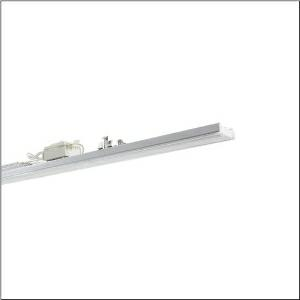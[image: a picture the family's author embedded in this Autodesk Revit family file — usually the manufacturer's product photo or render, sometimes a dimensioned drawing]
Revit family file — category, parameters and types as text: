
# Revit family: licross_21_recessed_ho_52te11cn4c5s
name_source: partatom
category: Lighting Fixtures
units: mm (PartAtom-declared; Revit-internal decimal feet)

## family parameters
Cut with Voids When Loaded = No
Host = Face
Light Source = No
Part Type = Normal
Room Calculation Point = No
Round Connector Dimension = Use Diameter
Shared = No

## types (1)
- --- (1 x LED, 12640 lm, 68.4 W, 4000K)
    Apparent Load = 68 VA
    CIE Flux Codes = 87 95 99 100 100
    Color Rendering = 80
    Color Temperature = 4000K
    Default Elevation = 1800 mm
    Description = Licross 21 Recessed HO, luminaire insert, of sheet steel, galvanised, coil coated, white, length: 1.500mm, width: 66mm, height: 67mm, LED rated luminous flux: 12.640lm, light colour: 840, SDCM (Standard Deviation of Colour Matching)MacAdam ≤ 3 SDCM (initial), control gear: ON/OFF Multilumen, CLOi, with plug, 3-pole, with phase selection, mains connection: 220..240V, AC, 50/60Hz, start of lifetime: 68W, end of service life: 83W, internal wiring halogen-free, primary light control with lens, of plastic, primary optical cover: cover, of PMMA, light emission: direct distribution, primary light characteristic: symmetric, protection rating (complete): IP54, insulation class (complete): insulation class I (protective earthing), certification: CE, ENEC, VDE, UKCA, protection symbol: D if used in an environment with non-conductive dust loads with corresponding accessories, impact resistance: IK06, permissible ambient temperature for indoor applications: -35..+30°C, corresponds to IFS (International Featured Standards) requirements for safety and quality in the food industry, reducing of maximum allowable ambient temperature of 5°C with ceiling mounting, LABS conformity tested according to VDMA 24364:2018-05, The light source and the operating device comply with the requirements of the Ecodesign Regulation (EU) 2019/2020 and are replaceable in accordance with this regulation, packaging unit: 1 piece
    Height = 58 mm
    Lamp = 1 x LED
    Lamp Light Flux = 12640 lm
    Lamp Power = 68.4 W
    Lamp count = 1
    Length = 1500 mm
    Luminous efficacy = 185 lm/W
    Manufacturer = Siteco
    ModVariant = No
    Model = 52TE11CN4C5S
    Mounting Place = Ceiling
    Mounting Type = Pendant
    Number of Poles = 1
    OnlyDefault = Yes
    Power Factor = 1
    Product Name = Licross 21 Recessed HO
    Product group = luminaire insert | ceiling pendant
    ProductGroupID = 901
    Protection Class = Protection class I
    Protection Degree = IP 54
    RLX_Detail_Level = 1
    RLX_Emergency_Light_Flux = 0 lm
    RLX_Emergency_Type = 0
    RLX_Emergency_Type_DB = No
    RlxData = <blob elided: 22581 chars, md5=9d481bde>
    Socket = socket
    Standby Power = 0 W
    System Light Flux = 12640 lm
    System Power = 68 W
    Type Comments = factory setting: luminous flux: 100 % | (A | C | E) | 161 mA
    Type Image = l_1296930.jpg
    URL = http://relux.com
    VarID = @adj_110649
    Voltage = 0 V
    Weight = 0.00 kg
    Width = 66 mm

## geometry (parser evidence)
native form markers: Blend x4, Sweep x11
no freeform markers — native parametric forms only
